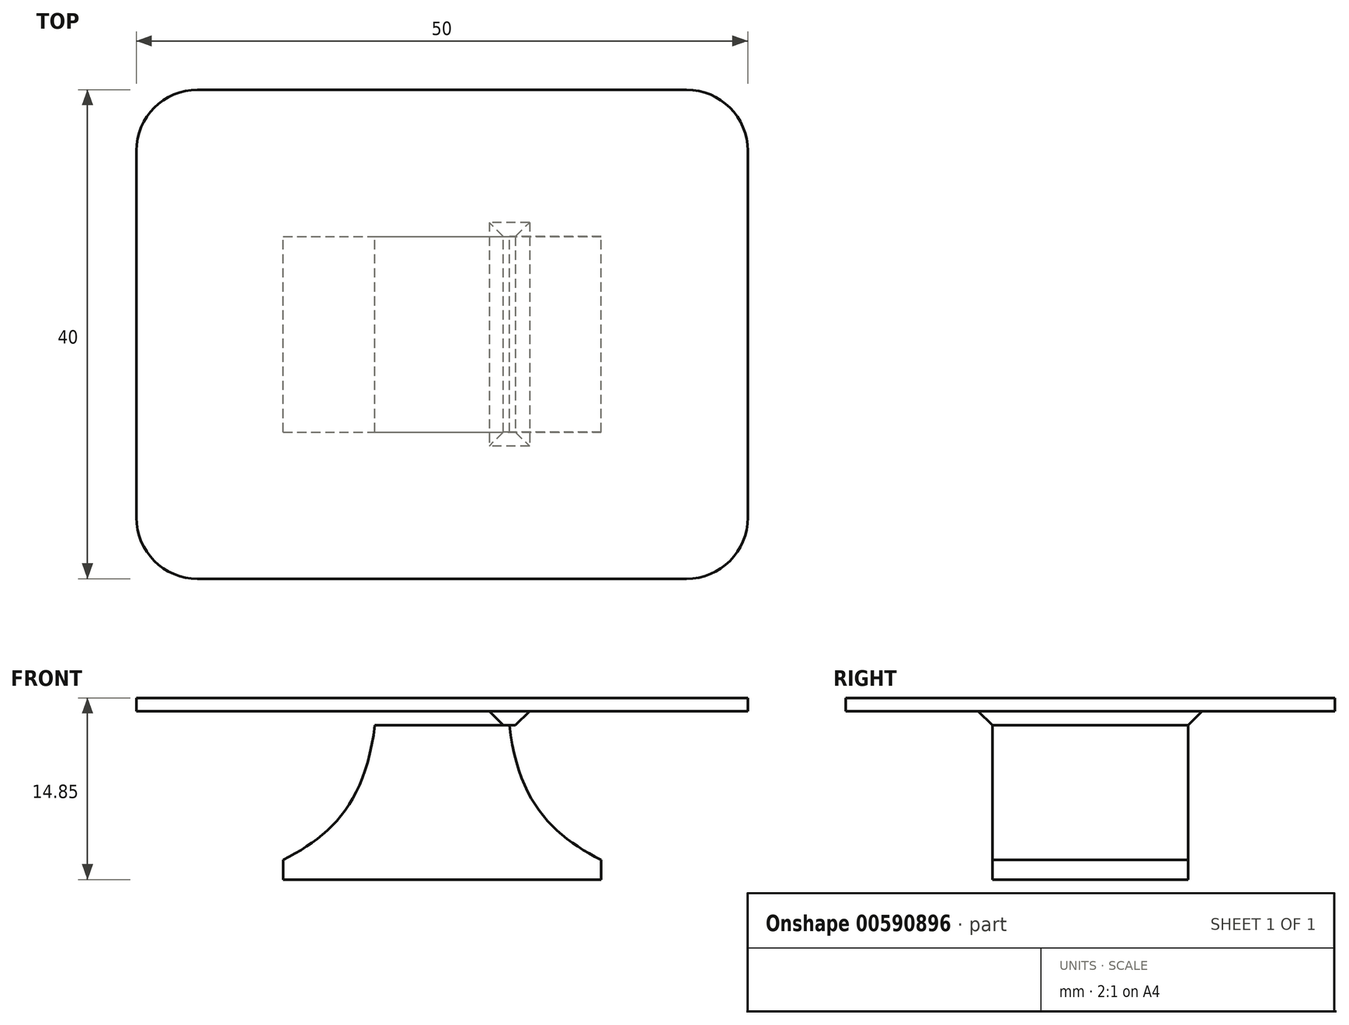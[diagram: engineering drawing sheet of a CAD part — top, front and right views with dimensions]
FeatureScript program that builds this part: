
annotation { "Feature Type Name" : "Feature", "Feature Type Description" : "" }
export const myFeature = defineFeature(function(context is Context, id is Id, definition is map)
    precondition{}
    {
        {
            var Q0;
            Q0=qCreatedBy(makeId("Front.planeOp"),FACE);
            var sketch = newSketch(context, id + "F0", { "sketchPlane" : qUnion([Q0])});
            skLineSegment(sketch, "E0.bottom", {"start": v(0, 14.85) * mm, "end": v(-25, 14.85) * mm});
            skLineSegment(sketch, "E0.top", {"start": v(0, 13.77) * mm, "end": v(-25, 13.77) * mm});
            skLineSegment(sketch, "E0.left", {"start": v(0, 14.85) * mm, "end": v(0, 13.77) * mm});
            skLineSegment(sketch, "E0.right", {"start": v(-25, 14.85) * mm, "end": v(-25, 13.77) * mm});
            skLineSegment(sketch, "E1.bottom", {"start": v(-11, 13.77) * mm, "end": v(0, 13.77) * mm});
            skLineSegment(sketch, "E1.top", {"start": v(-11, 12.62) * mm, "end": v(0, 12.62) * mm});
            skLineSegment(sketch, "E1.left", {"start": v(-11, 13.77) * mm, "end": v(-11, 12.62) * mm});
            skLineSegment(sketch, "E1.right", {"start": v(0, 13.77) * mm, "end": v(0, 12.62) * mm});
            skLineSegment(sketch, "E2.bottom", {"start": v(-13, 1.62) * mm, "end": v(0, 1.62) * mm});
            skLineSegment(sketch, "E2.top", {"start": v(-13, 0) * mm, "end": v(0, 0) * mm});
            skLineSegment(sketch, "E2.left", {"start": v(-13, 1.62) * mm, "end": v(-13, 0) * mm});
            skLineSegment(sketch, "E2.right", {"start": v(0, 1.62) * mm, "end": v(0, 0) * mm});
            skFitSpline(sketch, "E3", {"points": [v(-13, 1.62) * mm, v(-5.5, 12.62) * mm], "startDerivative": vector(11.48, 5.74) * mm, "endDerivative": vector(2.28, 19.2) * mm});
            skLineSegment(sketch, "E4", {"start": v(0, 14.85) * mm, "end": v(0, 0) * mm});
            skLineSegment(sketch, "E5.MirrorCS", {"start": v(13, 1.62) * mm, "end": v(13, 0) * mm});
            skLineSegment(sketch, "E6.MirrorCS", {"start": v(25, 14.85) * mm, "end": v(25, 13.77) * mm});
            skLineSegment(sketch, "E7.MirrorCS", {"start": v(11, 13.77) * mm, "end": v(11, 12.62) * mm});
            skFitSpline(sketch, "E8.MirrorCS", {"points": [v(13, 1.62) * mm, v(5.5, 12.62) * mm], "startDerivative": vector(-11.48, 5.74) * mm, "endDerivative": vector(-2.28, 19.2) * mm});
            skLineSegment(sketch, "E9.MirrorCS", {"start": v(13, 1.62) * mm, "end": v(0, 1.62) * mm});
            skLineSegment(sketch, "E10.MirrorCS", {"start": v(13, 0) * mm, "end": v(0, 0) * mm});
            skLineSegment(sketch, "E11.MirrorCS", {"start": v(0, 14.85) * mm, "end": v(25, 14.85) * mm});
            skLineSegment(sketch, "E12.MirrorCS", {"start": v(0, 13.77) * mm, "end": v(25, 13.77) * mm});
            skLineSegment(sketch, "E13.MirrorCS", {"start": v(11, 12.62) * mm, "end": v(0, 12.62) * mm});
            skLineSegment(sketch, "E14.MirrorCS", {"start": v(11, 13.77) * mm, "end": v(0, 13.77) * mm});
            skSolve(sketch);
        }
        {
            var Q0;
            Q0=makeQuery(id+"F0.imprint","IMPRINT",FACE,{"disambiguationData":[TD([[makeQuery(id+"F0.imprint","IMPRINT",EDGE,{"derivedFrom":sQuery(id+"F0.wireOp",EDGE,"E0.bottom")}),1.0]])]});
            var Q1;
            Q1=makeQuery(id+"F0.imprint","IMPRINT",FACE,{"disambiguationData":[TD([[makeQuery(id+"F0.imprint","IMPRINT",EDGE,{"derivedFrom":sQuery(id+"F0.wireOp",EDGE,"E0.left")}),1.0]])]});
            extrude(context, id + "F1", {"entities" : qUnion([Q0, Q1]), "endBound" : BoundingType.SYMMETRIC, "depth" : 40 * mm, "offsetDistance" : 25 * mm});
        }
        {
            var Q0;
            Q0=makeQuery(id+"F0.imprint","IMPRINT",FACE,{"disambiguationData":[TD([[makeQuery(id+"F0.imprint","IMPRINT",EDGE,{"derivedFrom":sQuery(id+"F0.wireOp",EDGE,"E1.bottom")}),-1.0]])]});
            var Q1;
            {var subQ3=sQuery(id+"F0.wireOp",EDGE,"E7.MirrorCS");Q1=makeQuery(id+"F0.imprint","IMPRINT",FACE,{"disambiguationData":[TD([[makeQuery(id+"F0.imprint","IMPRINT",EDGE,{"derivedFrom":subQ3}),-1.0]])]});}
            var Q2;
            Q2=makeQuery(id+"F0.imprint","IMPRINT",FACE,{"disambiguationData":[TD([[makeQuery(id+"F0.imprint","IMPRINT",EDGE,{"derivedFrom":sQuery(id+"F0.wireOp",EDGE,"E2.bottom")}),-1.0]])]});
            var Q3;
            Q3=makeQuery(id+"F0.imprint","IMPRINT",FACE,{"disambiguationData":[TD([[makeQuery(id+"F0.imprint","IMPRINT",EDGE,{"derivedFrom":sQuery(id+"F0.wireOp",EDGE,"E5.MirrorCS")}),-1.0]])]});
            extrude(context, id + "F2", {"entities" : qUnion([Q0, Q1, Q2, Q3]), "operationType" : NewBodyOperationType.ADD, "endBound" : BoundingType.SYMMETRIC, "depth" : 26 * mm, "offsetDistance" : 25 * mm});
        }
        {
            var Q0;
            Q0=makeQuery(id+"F2.opExtrude","CAP_EDGE",EDGE,{"disambiguationData":[OSD([sQuery(id+"F0.wireOp",EDGE,"E1.top"),sQuery(id+"F0.wireOp",EDGE,"E13.MirrorCS")])],"isStart":true});
            var Q1;
            Q1=makeQuery(id+"F2.opExtrude","SWEPT_EDGE",EDGE,{"disambiguationData":[OSD([sQuery(id+"F0.wireOp",EDGE,"E1.top"),sQuery(id+"F0.wireOp",EDGE,"E1.left")])]});
            var Q2;
            Q2=makeQuery(id+"F2.opExtrude","SWEPT_EDGE",EDGE,{"disambiguationData":[OSD([sQuery(id+"F0.wireOp",EDGE,"E7.MirrorCS"),sQuery(id+"F0.wireOp",EDGE,"E13.MirrorCS")])]});
            var Q3;
            Q3=makeQuery(id+"F2.opExtrude","CAP_EDGE",EDGE,{"disambiguationData":[OSD([sQuery(id+"F0.wireOp",EDGE,"E1.top"),sQuery(id+"F0.wireOp",EDGE,"E13.MirrorCS")])],"isStart":false});
            chamfer(context, id + "F3", {"entities" : qUnion([Q0, Q1, Q2, Q3]), "width" : 5 * mm, "tangentPropagation" : true});
        }
        {
            var Q0;
            Q0=makeQuery(id+"F2.opExtrude","CAP_EDGE",EDGE,{"disambiguationData":[OSD([sQuery(id+"F0.wireOp",EDGE,"E2.left")])],"isStart":true});
            var Q1;
            Q1=makeQuery(id+"F2.opExtrude","CAP_EDGE",EDGE,{"disambiguationData":[OSD([sQuery(id+"F0.wireOp",EDGE,"E2.left")])],"isStart":false});
            var Q2;
            Q2=makeQuery(id+"F2.opExtrude","CAP_EDGE",EDGE,{"disambiguationData":[OSD([sQuery(id+"F0.wireOp",EDGE,"E5.MirrorCS")])],"isStart":false});
            var Q3;
            Q3=makeQuery(id+"F2.opExtrude","CAP_EDGE",EDGE,{"disambiguationData":[OSD([sQuery(id+"F0.wireOp",EDGE,"E5.MirrorCS")])],"isStart":true});
            fillet(context, id + "F4", {"entities" : qUnion([Q0, Q1, Q2, Q3]), "radius" : 5 * mm, "tangentPropagation" : true, "allowEdgeOverflow" : false});
        }
        {
            var Q0;
            Q0=makeQuery(id+"F1.opExtrude","CAP_EDGE",EDGE,{"disambiguationData":[OSD([sQuery(id+"F0.wireOp",EDGE,"E0.right")])],"isStart":false});
            var Q1;
            Q1=makeQuery(id+"F1.opExtrude","CAP_EDGE",EDGE,{"disambiguationData":[OSD([sQuery(id+"F0.wireOp",EDGE,"E0.right")])],"isStart":true});
            var Q2;
            Q2=makeQuery(id+"F1.opExtrude","CAP_EDGE",EDGE,{"disambiguationData":[OSD([sQuery(id+"F0.wireOp",EDGE,"E6.MirrorCS")])],"isStart":false});
            var Q3;
            Q3=makeQuery(id+"F1.opExtrude","CAP_EDGE",EDGE,{"disambiguationData":[OSD([sQuery(id+"F0.wireOp",EDGE,"E6.MirrorCS")])],"isStart":true});
            fillet(context, id + "F5", {"entities" : qUnion([Q0, Q1, Q2, Q3]), "radius" : 5 * mm, "tangentPropagation" : true, "allowEdgeOverflow" : false});
        }
        {
            var Q0;
            Q0=makeQuery(id+"F2.opExtrude","SWEPT_BODY",BODY,{"disambiguationData":[OSD([sQuery(id+"F0.wireOp",EDGE,"E2.bottom"),sQuery(id+"F0.wireOp",EDGE,"E2.top"),sQuery(id+"F0.wireOp",EDGE,"E2.left"),sQuery(id+"F0.wireOp",EDGE,"E5.MirrorCS"),sQuery(id+"F0.wireOp",EDGE,"E9.MirrorCS"),sQuery(id+"F0.wireOp",EDGE,"E10.MirrorCS")])]});
            deleteBodies(context, id + "F6", {"entities" : qUnion([Q0])});
        }
        {
            var Q0;
            Q0=makeQuery(id+"F0.imprint","IMPRINT",FACE,{"disambiguationData":[TD([[makeQuery(id+"F0.imprint","IMPRINT",EDGE,{"derivedFrom":sQuery(id+"F0.wireOp",EDGE,"E2.bottom")}),1.0]])]});
            var Q1;
            Q1=makeQuery(id+"F0.imprint","IMPRINT",FACE,{"disambiguationData":[TD([[makeQuery(id+"F0.imprint","IMPRINT",EDGE,{"derivedFrom":sQuery(id+"F0.wireOp",EDGE,"E2.bottom")}),-1.0]])]});
            var Q2;
            {var subQ0=sQuery(id+"F0.wireOp",EDGE,"E4");Q2=makeQuery(id+"F0.imprint","IMPRINT",FACE,{"disambiguationData":[TD([[makeQuery(id+"F0.imprint","IMPRINT",EDGE,{"derivedFrom":subQ0}),1.0]])]});}
            var Q3;
            Q3=makeQuery(id+"F0.imprint","IMPRINT",FACE,{"disambiguationData":[TD([[makeQuery(id+"F0.imprint","IMPRINT",EDGE,{"derivedFrom":sQuery(id+"F0.wireOp",EDGE,"E5.MirrorCS")}),-1.0]])]});
            extrude(context, id + "F7", {"entities" : qUnion([Q0, Q1, Q2, Q3]), "operationType" : NewBodyOperationType.ADD, "endBound" : BoundingType.SYMMETRIC, "depth" : 16 * mm, "offsetDistance" : 25 * mm});
        }
    });
